# Revit family: Distanzmuffe rund
name_source: partatom
category: HLS-Bauteile
revit_build: Autodesk Revit 2017 (Build: 20190507_1515(x64)
units: mm (PartAtom-declared; Revit-internal decimal feet)

## family parameters
Arbeitsebenenbasiert = Nein
Beim Laden mit Abzugskörper schneiden = Nein
Bemaßung runder Anschluss = Durchmesser verwenden
Gemeinsam genutzt = Ja
Immer vertikal = Nein
Raumberechnungspunkt = Nein
Teiletyp = Normal

## types (4) — shared parameters
Fabrikat = MEFA
Firma = MEFA Befestigungs- und Montagesysteme GmbH
Kurztext1 = Distanzmuffe rund
Material = Stahl
Mengeneinheit = St
Oberflaeche = galvanisch verzinkt
vpe = 100 St

## per-type parameters (varying)
| type | Artikelnummer | Außendurchmesser | D | D0 | EAN | Gewicht | Gewicht pro Bauteil | Innengewinde 1 | Kurztext2 | Länge | Länge Innengewinde 1 |
| Distanzmuffe rund M 6 L= 25 | 0700010 | 10 mm  [stored 0.0328084 ft] | 10 mm  [stored 0.0328084 ft] | 5 mm  [stored 0.0164042 ft] | 4250928415974 | 0.01 kg | 0.01 kg | M6 | Innengew. M6 L= 25 mm | 25 mm  [stored 0.082021 ft] | 25 mm |
| Distanzmuffe rund M 8 L= 30 | 0700029 | 11 mm  [stored 0.0360892 ft] | 11 mm  [stored 0.0360892 ft] | 7 mm  [stored 0.0229659 ft] | 4250928416025 | 0.01 kg | 0.01 kg | M8 | Innengew. M8 L= 30 mm | 30 mm  [stored 0.0984252 ft] | 30 mm |
| Distanzmuffe rund M10 L= 40 | 0700037 | 13 mm | 13 mm | 8 mm  [stored 0.0262467 ft] | 4250928416032 | 0.02 kg | 0.02 kg | M10 | Innengew. M10 L= 40 mm | 40 mm  [stored 0.131234 ft] | 40 mm |
| Distanzmuffe rund M12 L= 40 | 0700045 | 15 mm  [stored 0.0492126 ft] | 15 mm  [stored 0.0492126 ft] | 10 mm  [stored 0.0328084 ft] | 4250928416049 | 0.03 kg | 0.03 kg | M12 | Innengew. M12 L= 40 mm | 40 mm  [stored 0.131234 ft] | 40 mm |

note: [stored X ft] marks values corroborated as IEEE doubles in the binary element streams (Revit-internal decimal feet)
